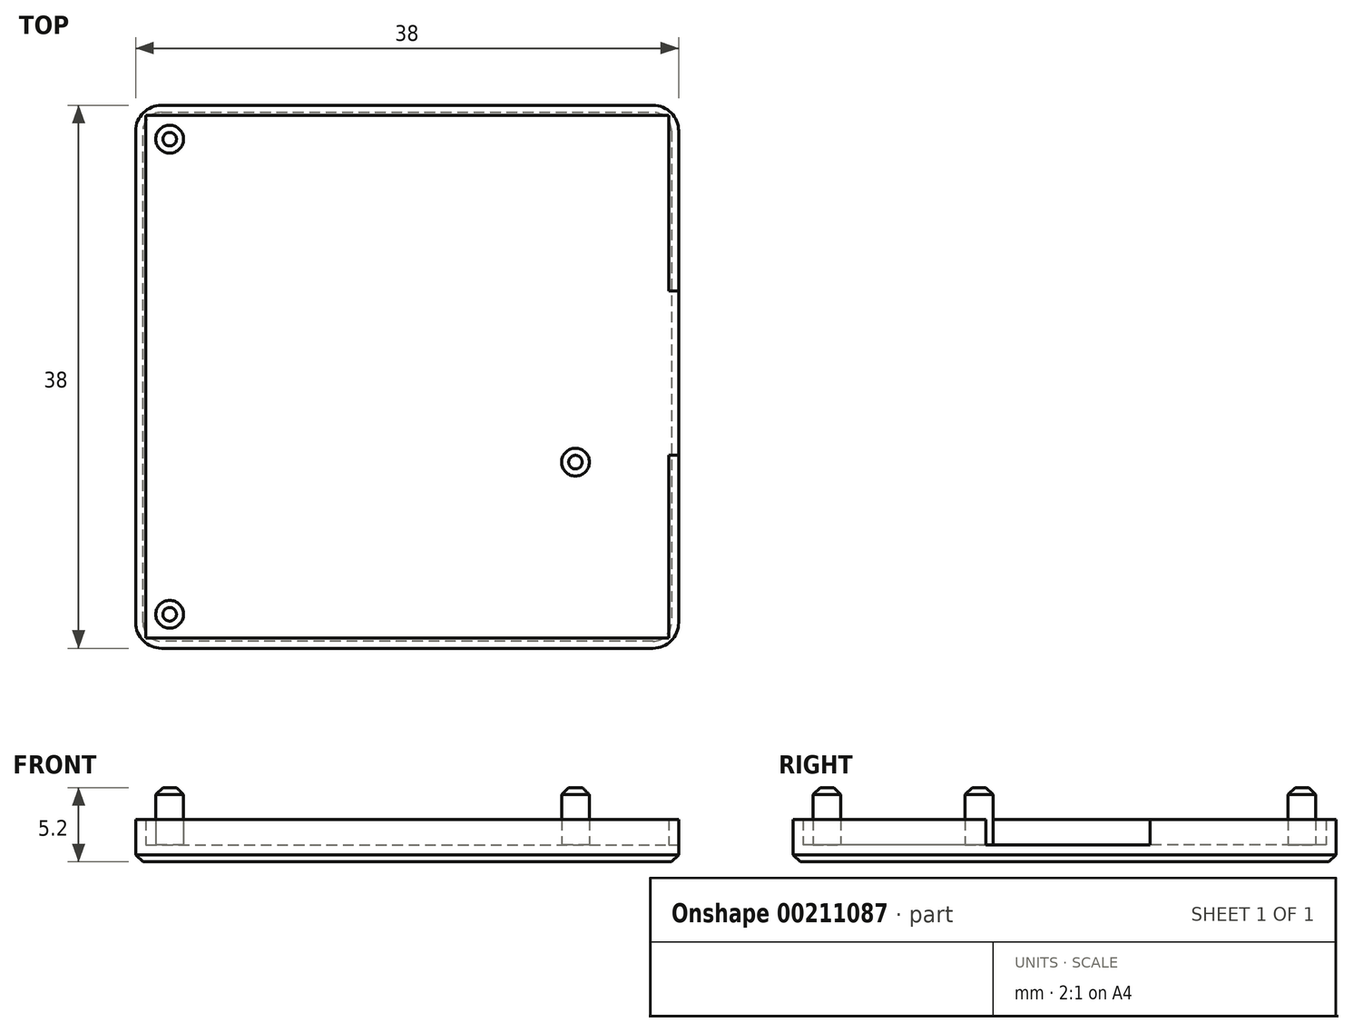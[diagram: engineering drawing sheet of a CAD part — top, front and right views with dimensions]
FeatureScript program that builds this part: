
annotation { "Feature Type Name" : "Feature", "Feature Type Description" : "" }
export const myFeature = defineFeature(function(context is Context, id is Id, definition is map)
    precondition{}
    {
        {
            var Q0;
            Q0=qCreatedBy(makeId("Top.planeOp"),FACE);
            var sketch = newSketch(context, id + "F0", { "sketchPlane" : qUnion([Q0])});
            skLineSegment(sketch, "E0.bottom", {"start": v(19, 19) * mm, "end": v(-19, 19) * mm});
            skLineSegment(sketch, "E0.top", {"start": v(19, -19) * mm, "end": v(-19, -19) * mm});
            skLineSegment(sketch, "E0.left", {"start": v(19, 19) * mm, "end": v(19, -19) * mm});
            skLineSegment(sketch, "E0.right", {"start": v(-19, 19) * mm, "end": v(-19, -19) * mm});
            skPoint(sketch, "E0.middle", {"position": v(0, 0) * mm});
            skCircle(sketch, "E1", {"center": v(-16.63, 16.62) * mm, "radius": 0.97 * mm});
            skCircle(sketch, "E2", {"center": v(11.77, -5.98) * mm, "radius": 0.97 * mm});
            skCircle(sketch, "E3", {"center": v(-16.63, -16.62) * mm, "radius": 0.97 * mm});
            skLineSegment(sketch, "E4", {"start": v(-19, 18.3) * mm, "end": v(19, 18.3) * mm});
            skLineSegment(sketch, "E5", {"start": v(-18.3, 19) * mm, "end": v(-18.3, -19) * mm});
            skLineSegment(sketch, "E6", {"start": v(-19, -18.3) * mm, "end": v(19, -18.3) * mm});
            skLineSegment(sketch, "E7", {"start": v(18.3, 19) * mm, "end": v(18.3, -19) * mm});
            skLineSegment(sketch, "E8", {"start": v(18.3, 6) * mm, "end": v(19, 6) * mm});
            skLineSegment(sketch, "E9", {"start": v(18.3, -5.5) * mm, "end": v(19, -5.5) * mm});
            skSolve(sketch);
        }
        {
            var Q0;
            Q0=makeQuery(id+"F0.imprint","IMPRINT",FACE,{"disambiguationData":[TD([[makeQuery(id+"F0.imprint","IMPRINT",EDGE,{"derivedFrom":sQuery(id+"F0.wireOp",EDGE,"E2")}),1.0]])]});
            var Q1;
            Q1=makeQuery(id+"F0.imprint","IMPRINT",FACE,{"disambiguationData":[TD([[makeQuery(id+"F0.imprint","IMPRINT",EDGE,{"derivedFrom":sQuery(id+"F0.wireOp",EDGE,"E3")}),1.0]])]});
            var Q2;
            {var subQ0=sQuery(id+"F0.wireOp",EDGE,"E0.left");var subQ1=sQuery(id+"F0.wireOp",EDGE,"E0.bottom");var subQ2=makeQuery(id+"F0.imprint","INTERSECT",VERTEX,{"derivedFrom":[subQ1,subQ0]});Q2=makeQuery(id+"F0.imprint","IMPRINT",FACE,{"disambiguationData":[TD([[makeQuery(id+"F0.imprint","IMPRINT",EDGE,{"disambiguationData":[TD([[subQ2,-1.0]])],"derivedFrom":subQ1}),1.0]])]});}
            var Q3;
            {var subQ0=sQuery(id+"F0.wireOp",EDGE,"E0.right");var subQ1=sQuery(id+"F0.wireOp",EDGE,"E0.bottom");var subQ2=makeQuery(id+"F0.imprint","INTERSECT",VERTEX,{"derivedFrom":[subQ1,subQ0]});Q3=makeQuery(id+"F0.imprint","IMPRINT",FACE,{"disambiguationData":[TD([[makeQuery(id+"F0.imprint","IMPRINT",EDGE,{"disambiguationData":[TD([[subQ2,1.0]])],"derivedFrom":subQ1}),1.0]])]});}
            var Q4;
            Q4=makeQuery(id+"F0.imprint","IMPRINT",FACE,{"disambiguationData":[TD([[makeQuery(id+"F0.imprint","IMPRINT",EDGE,{"derivedFrom":sQuery(id+"F0.wireOp",EDGE,"E1")}),1.0]])]});
            var Q5;
            {var subQ0=sQuery(id+"F0.wireOp",EDGE,"E0.left");var subQ1=sQuery(id+"F0.wireOp",EDGE,"E0.top");var subQ2=makeQuery(id+"F0.imprint","INTERSECT",VERTEX,{"derivedFrom":[subQ1,subQ0]});Q5=makeQuery(id+"F0.imprint","IMPRINT",FACE,{"disambiguationData":[TD([[makeQuery(id+"F0.imprint","IMPRINT",EDGE,{"disambiguationData":[TD([[subQ2,-1.0]])],"derivedFrom":subQ1}),-1.0]])]});}
            var Q6;
            {var subQ0=sQuery(id+"F0.wireOp",EDGE,"E0.right");var subQ1=sQuery(id+"F0.wireOp",EDGE,"E0.top");var subQ2=makeQuery(id+"F0.imprint","INTERSECT",VERTEX,{"derivedFrom":[subQ1,subQ0]});Q6=makeQuery(id+"F0.imprint","IMPRINT",FACE,{"disambiguationData":[TD([[makeQuery(id+"F0.imprint","IMPRINT",EDGE,{"disambiguationData":[TD([[subQ2,1.0]])],"derivedFrom":subQ1}),-1.0]])]});}
            var Q7;
            {var subQ0=sQuery(id+"F0.wireOp",EDGE,"E5");var subQ1=sQuery(id+"F0.wireOp",EDGE,"E0.bottom");var subQ2=makeQuery(id+"F0.imprint","INTERSECT",VERTEX,{"derivedFrom":[subQ1,subQ0]});Q7=makeQuery(id+"F0.imprint","IMPRINT",FACE,{"disambiguationData":[TD([[makeQuery(id+"F0.imprint","IMPRINT",EDGE,{"disambiguationData":[TD([[subQ2,1.0]])],"derivedFrom":subQ1}),1.0]])]});}
            var Q8;
            Q8=makeQuery(id+"F0.imprint","IMPRINT",FACE,{"disambiguationData":[TD([[makeQuery(id+"F0.imprint","IMPRINT",EDGE,{"derivedFrom":sQuery(id+"F0.wireOp",EDGE,"E1")}),-1.0]])]});
            var Q9;
            {var subQ0=sQuery(id+"F0.wireOp",EDGE,"E5");var subQ1=sQuery(id+"F0.wireOp",EDGE,"E0.top");var subQ2=makeQuery(id+"F0.imprint","INTERSECT",VERTEX,{"derivedFrom":[subQ1,subQ0]});Q9=makeQuery(id+"F0.imprint","IMPRINT",FACE,{"disambiguationData":[TD([[makeQuery(id+"F0.imprint","IMPRINT",EDGE,{"disambiguationData":[TD([[subQ2,1.0]])],"derivedFrom":subQ1}),-1.0]])]});}
            var Q10;
            {var subQ3=sQuery(id+"F0.wireOp",EDGE,"E8");Q10=makeQuery(id+"F0.imprint","IMPRINT",FACE,{"disambiguationData":[TD([[makeQuery(id+"F0.imprint","IMPRINT",EDGE,{"derivedFrom":subQ3}),1.0]])]});}
            var Q11;
            {var subQ0=sQuery(id+"F0.wireOp",EDGE,"E8");Q11=makeQuery(id+"F0.imprint","IMPRINT",FACE,{"disambiguationData":[TD([[makeQuery(id+"F0.imprint","IMPRINT",EDGE,{"derivedFrom":subQ0}),-1.0]])]});}
            var Q12;
            {var subQ3=sQuery(id+"F0.wireOp",EDGE,"E9");Q12=makeQuery(id+"F0.imprint","IMPRINT",FACE,{"disambiguationData":[TD([[makeQuery(id+"F0.imprint","IMPRINT",EDGE,{"derivedFrom":subQ3}),-1.0]])]});}
            var Q13;
            {var subQ0=sQuery(id+"F0.wireOp",EDGE,"E4");var subQ1=sQuery(id+"F0.wireOp",EDGE,"E0.right");var subQ2=makeQuery(id+"F0.imprint","INTERSECT",VERTEX,{"derivedFrom":[subQ1,subQ0]});Q13=makeQuery(id+"F0.imprint","IMPRINT",FACE,{"disambiguationData":[TD([[makeQuery(id+"F0.imprint","IMPRINT",EDGE,{"disambiguationData":[TD([[subQ2,-1.0]])],"derivedFrom":subQ1}),1.0]])]});}
            extrude(context, id + "F1", {"entities" : qUnion([Q0, Q1, Q2, Q3, Q4, Q5, Q6, Q7, Q8, Q9, Q10, Q11, Q12, Q13]), "oppositeDirection" : true, "depth" : 1.2 * mm});
        }
        {
            var Q0;
            {var subQ0=sQuery(id+"F0.wireOp",EDGE,"E5");var subQ1=sQuery(id+"F0.wireOp",EDGE,"E0.bottom");var subQ2=makeQuery(id+"F0.imprint","INTERSECT",VERTEX,{"derivedFrom":[subQ1,subQ0]});Q0=makeQuery(id+"F0.imprint","IMPRINT",FACE,{"disambiguationData":[TD([[makeQuery(id+"F0.imprint","IMPRINT",EDGE,{"disambiguationData":[TD([[subQ2,1.0]])],"derivedFrom":subQ1}),1.0]])]});}
            var Q1;
            {var subQ0=sQuery(id+"F0.wireOp",EDGE,"E0.right");var subQ1=sQuery(id+"F0.wireOp",EDGE,"E0.bottom");var subQ2=makeQuery(id+"F0.imprint","INTERSECT",VERTEX,{"derivedFrom":[subQ1,subQ0]});Q1=makeQuery(id+"F0.imprint","IMPRINT",FACE,{"disambiguationData":[TD([[makeQuery(id+"F0.imprint","IMPRINT",EDGE,{"disambiguationData":[TD([[subQ2,1.0]])],"derivedFrom":subQ1}),1.0]])]});}
            var Q2;
            {var subQ0=sQuery(id+"F0.wireOp",EDGE,"E0.left");var subQ1=sQuery(id+"F0.wireOp",EDGE,"E0.bottom");var subQ2=makeQuery(id+"F0.imprint","INTERSECT",VERTEX,{"derivedFrom":[subQ1,subQ0]});Q2=makeQuery(id+"F0.imprint","IMPRINT",FACE,{"disambiguationData":[TD([[makeQuery(id+"F0.imprint","IMPRINT",EDGE,{"disambiguationData":[TD([[subQ2,-1.0]])],"derivedFrom":subQ1}),1.0]])]});}
            var Q3;
            {var subQ3=sQuery(id+"F0.wireOp",EDGE,"E8");Q3=makeQuery(id+"F0.imprint","IMPRINT",FACE,{"disambiguationData":[TD([[makeQuery(id+"F0.imprint","IMPRINT",EDGE,{"derivedFrom":subQ3}),1.0]])]});}
            var Q4;
            {var subQ3=sQuery(id+"F0.wireOp",EDGE,"E9");Q4=makeQuery(id+"F0.imprint","IMPRINT",FACE,{"disambiguationData":[TD([[makeQuery(id+"F0.imprint","IMPRINT",EDGE,{"derivedFrom":subQ3}),-1.0]])]});}
            var Q5;
            {var subQ0=sQuery(id+"F0.wireOp",EDGE,"E0.left");var subQ1=sQuery(id+"F0.wireOp",EDGE,"E0.top");var subQ2=makeQuery(id+"F0.imprint","INTERSECT",VERTEX,{"derivedFrom":[subQ1,subQ0]});Q5=makeQuery(id+"F0.imprint","IMPRINT",FACE,{"disambiguationData":[TD([[makeQuery(id+"F0.imprint","IMPRINT",EDGE,{"disambiguationData":[TD([[subQ2,-1.0]])],"derivedFrom":subQ1}),-1.0]])]});}
            var Q6;
            {var subQ0=sQuery(id+"F0.wireOp",EDGE,"E5");var subQ1=sQuery(id+"F0.wireOp",EDGE,"E0.top");var subQ2=makeQuery(id+"F0.imprint","INTERSECT",VERTEX,{"derivedFrom":[subQ1,subQ0]});Q6=makeQuery(id+"F0.imprint","IMPRINT",FACE,{"disambiguationData":[TD([[makeQuery(id+"F0.imprint","IMPRINT",EDGE,{"disambiguationData":[TD([[subQ2,1.0]])],"derivedFrom":subQ1}),-1.0]])]});}
            var Q7;
            {var subQ0=sQuery(id+"F0.wireOp",EDGE,"E0.right");var subQ1=sQuery(id+"F0.wireOp",EDGE,"E0.top");var subQ2=makeQuery(id+"F0.imprint","INTERSECT",VERTEX,{"derivedFrom":[subQ1,subQ0]});Q7=makeQuery(id+"F0.imprint","IMPRINT",FACE,{"disambiguationData":[TD([[makeQuery(id+"F0.imprint","IMPRINT",EDGE,{"disambiguationData":[TD([[subQ2,1.0]])],"derivedFrom":subQ1}),-1.0]])]});}
            var Q8;
            {var subQ0=sQuery(id+"F0.wireOp",EDGE,"E4");var subQ1=sQuery(id+"F0.wireOp",EDGE,"E0.right");var subQ2=makeQuery(id+"F0.imprint","INTERSECT",VERTEX,{"derivedFrom":[subQ1,subQ0]});Q8=makeQuery(id+"F0.imprint","IMPRINT",FACE,{"disambiguationData":[TD([[makeQuery(id+"F0.imprint","IMPRINT",EDGE,{"disambiguationData":[TD([[subQ2,-1.0]])],"derivedFrom":subQ1}),1.0]])]});}
            extrude(context, id + "F2", {"entities" : qUnion([Q0, Q1, Q2, Q3, Q4, Q5, Q6, Q7, Q8]), "operationType" : NewBodyOperationType.ADD, "depth" : 1.75 * mm});
        }
        {
            var Q0;
            Q0=makeQuery(id+"F0.imprint","IMPRINT",FACE,{"disambiguationData":[TD([[makeQuery(id+"F0.imprint","IMPRINT",EDGE,{"derivedFrom":sQuery(id+"F0.wireOp",EDGE,"E1")}),1.0]])]});
            var Q1;
            Q1=makeQuery(id+"F0.imprint","IMPRINT",FACE,{"disambiguationData":[TD([[makeQuery(id+"F0.imprint","IMPRINT",EDGE,{"derivedFrom":sQuery(id+"F0.wireOp",EDGE,"E3")}),1.0]])]});
            var Q2;
            Q2=makeQuery(id+"F0.imprint","IMPRINT",FACE,{"disambiguationData":[TD([[makeQuery(id+"F0.imprint","IMPRINT",EDGE,{"derivedFrom":sQuery(id+"F0.wireOp",EDGE,"E2")}),1.0]])]});
            extrude(context, id + "F3", {"entities" : qUnion([Q0, Q1, Q2]), "operationType" : NewBodyOperationType.ADD, "depth" : 4 * mm});
        }
        {
            var Q0;
            {var subQ0=sQuery(id+"F0.wireOp",EDGE,"E0.right");var subQ1=sQuery(id+"F0.wireOp",EDGE,"E0.bottom");Q0=makeQuery(id+"F2.boolean.opBoolean","MERGE",EDGE,{"derivedFrom":[makeQuery(id+"F1.opExtrude","SWEPT_EDGE",EDGE,{"disambiguationData":[OSD([subQ1,subQ0])]}),makeQuery(id+"F2.opExtrude","SWEPT_EDGE",EDGE,{"disambiguationData":[OSD([subQ1,subQ0])]})]});}
            var Q1;
            {var subQ0=sQuery(id+"F0.wireOp",EDGE,"E0.left");var subQ1=sQuery(id+"F0.wireOp",EDGE,"E0.bottom");Q1=makeQuery(id+"F2.boolean.opBoolean","MERGE",EDGE,{"derivedFrom":[makeQuery(id+"F1.opExtrude","SWEPT_EDGE",EDGE,{"disambiguationData":[OSD([subQ1,subQ0])]}),makeQuery(id+"F2.opExtrude","SWEPT_EDGE",EDGE,{"disambiguationData":[OSD([subQ1,subQ0])]})]});}
            var Q2;
            {var subQ0=sQuery(id+"F0.wireOp",EDGE,"E0.right");var subQ1=sQuery(id+"F0.wireOp",EDGE,"E0.top");Q2=makeQuery(id+"F2.boolean.opBoolean","MERGE",EDGE,{"derivedFrom":[makeQuery(id+"F1.opExtrude","SWEPT_EDGE",EDGE,{"disambiguationData":[OSD([subQ1,subQ0])]}),makeQuery(id+"F2.opExtrude","SWEPT_EDGE",EDGE,{"disambiguationData":[OSD([subQ1,subQ0])]})]});}
            var Q3;
            {var subQ0=sQuery(id+"F0.wireOp",EDGE,"E0.left");var subQ1=sQuery(id+"F0.wireOp",EDGE,"E0.top");Q3=makeQuery(id+"F2.boolean.opBoolean","MERGE",EDGE,{"derivedFrom":[makeQuery(id+"F1.opExtrude","SWEPT_EDGE",EDGE,{"disambiguationData":[OSD([subQ1,subQ0])]}),makeQuery(id+"F2.opExtrude","SWEPT_EDGE",EDGE,{"disambiguationData":[OSD([subQ1,subQ0])]})]});}
            fillet(context, id + "F4", {"entities" : qUnion([Q0, Q1, Q2, Q3]), "radius" : 1.8 * mm, "tangentPropagation" : true, "allowEdgeOverflow" : false});
        }
        {
            var Q0;
            Q0=makeQuery(id+"F1.opExtrude","CAP_EDGE",EDGE,{"disambiguationData":[OSD([sQuery(id+"F0.wireOp",EDGE,"E0.top")])],"isStart":false});
            var Q1;
            Q1=makeQuery(id+"F3.opExtrude","CAP_EDGE",EDGE,{"disambiguationData":[OSD([sQuery(id+"F0.wireOp",EDGE,"E2")])],"isStart":false});
            var Q2;
            Q2=makeQuery(id+"F3.opExtrude","CAP_EDGE",EDGE,{"disambiguationData":[OSD([sQuery(id+"F0.wireOp",EDGE,"E1")])],"isStart":false});
            var Q3;
            Q3=makeQuery(id+"F3.opExtrude","CAP_EDGE",EDGE,{"disambiguationData":[OSD([sQuery(id+"F0.wireOp",EDGE,"E3")])],"isStart":false});
            var Q4;
            Q4=makeQuery(id+"F3.opExtrude","CAP_EDGE",EDGE,{"disambiguationData":[OSD([sQuery(id+"F0.wireOp",EDGE,"E1")])],"isStart":true});
            var Q5;
            Q5=makeQuery(id+"F3.opExtrude","CAP_EDGE",EDGE,{"disambiguationData":[OSD([sQuery(id+"F0.wireOp",EDGE,"E2")])],"isStart":true});
            var Q6;
            Q6=makeQuery(id+"F3.opExtrude","CAP_EDGE",EDGE,{"disambiguationData":[OSD([sQuery(id+"F0.wireOp",EDGE,"E3")])],"isStart":true});
            chamfer(context, id + "F5", {"entities" : qUnion([Q0, Q1, Q2, Q3, Q4, Q5, Q6]), "width" : .5 * mm, "tangentPropagation" : true});
        }
    });
